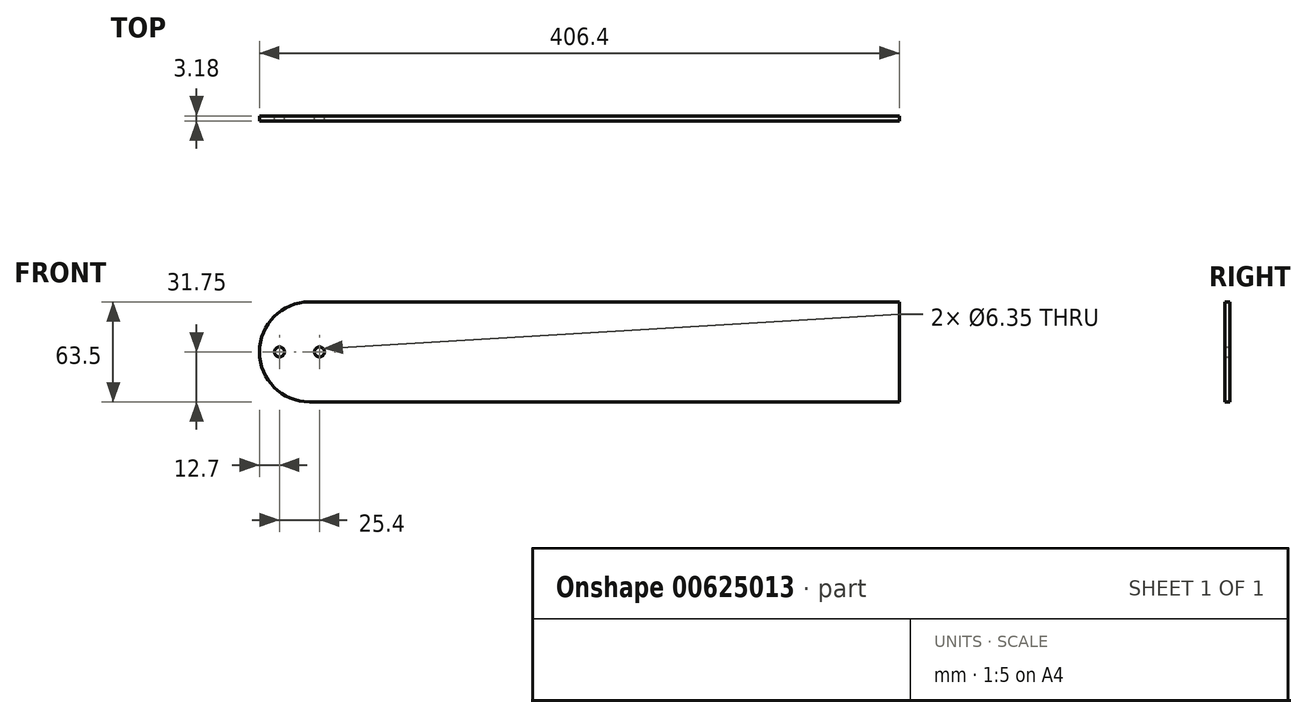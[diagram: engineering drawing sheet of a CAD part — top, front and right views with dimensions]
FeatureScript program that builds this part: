
annotation { "Feature Type Name" : "Feature", "Feature Type Description" : "" }
export const myFeature = defineFeature(function(context is Context, id is Id, definition is map)
    precondition{}
    {
        {
            var Q0;
            Q0=qCreatedBy(makeId("Front.planeOp"),FACE);
            var sketch = newSketch(context, id + "F0", { "sketchPlane" : qUnion([Q0])});
            skLineSegment(sketch, "E0.bottom", {"start": v(31.75, 0) * mm, "end": v(406.4, 0) * mm});
            skLineSegment(sketch, "E0.top", {"start": v(31.75, 63.5) * mm, "end": v(406.4, 63.5) * mm});
            skLineSegment(sketch, "E0.left", {"start": v(0, 31.75) * mm, "end": v(0, 31.75) * mm});
            skLineSegment(sketch, "E0.right", {"start": v(406.4, 0) * mm, "end": v(406.4, 63.5) * mm});
            skLineSegment(sketch, "E1", {"start": v(0, 31.75) * mm, "end": v(38.1, 31.75) * mm});
            skPoint(sketch, "E1.endSnap0", {"position": v(0, 31.75) * mm});
            skCircle(sketch, "E2", {"center": v(38.1, 31.75) * mm, "radius": 3.18 * mm});
            skCircle(sketch, "E3", {"center": v(38.1, 31.75) * mm, "radius": 25.4 * mm});
            skLineSegment(sketch, "E4", {"start": v(12.7, 31.75) * mm, "end": v(38.1, 31.75) * mm});
            skCircle(sketch, "E5", {"center": v(368.3, 31.75) * mm, "radius": 50 * mm});
            skCircle(sketch, "E6", {"center": v(368.3, 81.75) * mm, "radius": 6.35 * mm});
            skCircle(sketch, "E7", {"center": v(368.3, -18.25) * mm, "radius": 6.35 * mm});
            skCircle(sketch, "E8", {"center": v(318.3, 31.75) * mm, "radius": 6.35 * mm});
            skCircle(sketch, "E9", {"center": v(418.3, 31.75) * mm, "radius": 6.35 * mm});
            skPoint(sketch, "E10.visualSharp", {"position": v(0, 63.5) * mm});
            skArc(sketch, "E10.filletArc", {"start": v(31.75, 63.5) * mm, "mid": v(9.3, 54.2) * mm, "end": v(0, 31.75) * mm});
            skPoint(sketch, "E11.visualSharp", {"position": v(0, 0) * mm});
            skArc(sketch, "E11.filletArc", {"start": v(0, 31.75) * mm, "mid": v(9.3, 9.3) * mm, "end": v(31.75, 0) * mm});
            skCircle(sketch, "E12", {"center": v(12.7, 31.75) * mm, "radius": 3.18 * mm});
            skSolve(sketch);
        }
        {
            var Q0;
            {var subQ0=sQuery(id+"F0.wireOp",EDGE,"O3syXbHt-yHTN-aNau-WEg2-3ZSHqx7OYMuC");var subQ3=sQuery(id+"F0.wireOp",EDGE,"E0.top");var subQ4=makeQuery(id+"F0.imprint","INTERSECT",VERTEX,{"disambiguationData":[OD(0.0)],"derivedFrom":[subQ3,subQ0]});Q0=makeQuery(id+"F0.imprint","IMPRINT",FACE,{"disambiguationData":[TD([[makeQuery(id+"F0.imprint","IMPRINT",EDGE,{"disambiguationData":[TD([[subQ4,-1.0]])],"derivedFrom":subQ3}),-1.0]])]});}
            var Q1;
            {var subQ1=sQuery(id+"F0.wireOp",EDGE,"E0.bottom");var subQ5=sQuery(id+"F0.wireOp",EDGE,"O3syXbHt-yHTN-aNau-WEg2-3ZSHqx7OYMuC");var subQ8=makeQuery(id+"F0.imprint","INTERSECT",VERTEX,{"disambiguationData":[OD(0.0)],"derivedFrom":[subQ1,subQ5]});Q1=makeQuery(id+"F0.imprint","IMPRINT",FACE,{"disambiguationData":[TD([[makeQuery(id+"F0.imprint","IMPRINT",EDGE,{"disambiguationData":[TD([[subQ8,-1.0]])],"derivedFrom":subQ1}),1.0]])]});}
            var Q2;
            Q2=makeQuery(id+"F0.imprint","IMPRINT",FACE,{"disambiguationData":[TD([[makeQuery(id+"F0.imprint","IMPRINT",EDGE,{"derivedFrom":sQuery(id+"F0.wireOp",EDGE,"E2")}),-1.0]])]});
            var Q3;
            {var subQ0=sQuery(id+"F0.wireOp",EDGE,"O3syXbHt-yHTN-aNau-WEg2-3ZSHqx7OYMuC");var subQ1=sQuery(id+"F0.wireOp",EDGE,"E0.bottom");var subQ2=makeQuery(id+"F0.imprint","INTERSECT",VERTEX,{"disambiguationData":[OD(1.0)],"derivedFrom":[subQ1,subQ0]});Q3=makeQuery(id+"F0.imprint","IMPRINT",FACE,{"disambiguationData":[TD([[makeQuery(id+"F0.imprint","IMPRINT",EDGE,{"disambiguationData":[TD([[subQ2,1.0]])],"derivedFrom":subQ1}),1.0]])]});}
            var Q4;
            {var subQ0=sQuery(id+"F0.wireOp",EDGE,"O3syXbHt-yHTN-aNau-WEg2-3ZSHqx7OYMuC");var subQ1=sQuery(id+"F0.wireOp",EDGE,"E0.bottom");var subQ2=makeQuery(id+"F0.imprint","INTERSECT",VERTEX,{"disambiguationData":[OD(1.0)],"derivedFrom":[subQ1,subQ0]});Q4=makeQuery(id+"F0.imprint","IMPRINT",FACE,{"disambiguationData":[TD([[makeQuery(id+"F0.imprint","IMPRINT",EDGE,{"disambiguationData":[TD([[subQ2,-1.0]])],"derivedFrom":subQ1}),1.0]])]});}
            var Q5;
            {var subQ5=sQuery(id+"F0.wireOp",EDGE,"E0.right");Q5=makeQuery(id+"F0.imprint","IMPRINT",FACE,{"disambiguationData":[TD([[makeQuery(id+"F0.imprint","IMPRINT",EDGE,{"derivedFrom":subQ5}),1.0]])]});}
            var Q6;
            {var subQ0=sQuery(id+"F0.wireOp",EDGE,"E8");var subQ1=sQuery(id+"F0.wireOp",EDGE,"E5");var subQ2=makeQuery(id+"F0.imprint","INTERSECT",VERTEX,{"disambiguationData":[OD(0.0)],"derivedFrom":[subQ1,subQ0]});Q6=makeQuery(id+"F0.imprint","IMPRINT",FACE,{"disambiguationData":[TD([[makeQuery(id+"F0.imprint","IMPRINT",EDGE,{"disambiguationData":[TD([[subQ2,-1.0]])],"derivedFrom":subQ1}),1.0]])]});}
            var Q7;
            {var subQ0=sQuery(id+"F0.wireOp",EDGE,"E8");var subQ1=sQuery(id+"F0.wireOp",EDGE,"E5");var subQ2=makeQuery(id+"F0.imprint","INTERSECT",VERTEX,{"disambiguationData":[OD(0.0)],"derivedFrom":[subQ1,subQ0]});Q7=makeQuery(id+"F0.imprint","IMPRINT",FACE,{"disambiguationData":[TD([[makeQuery(id+"F0.imprint","IMPRINT",EDGE,{"disambiguationData":[TD([[subQ2,-1.0]])],"derivedFrom":subQ1}),-1.0]])]});}
            var Q8;
            {var subQ11=sQuery(id+"F0.wireOp",EDGE,"E10.filletArc");Q8=makeQuery(id+"F0.imprint","IMPRINT",FACE,{"disambiguationData":[TD([[makeQuery(id+"F0.imprint","IMPRINT",EDGE,{"derivedFrom":subQ11}),1.0]])]});}
            extrude(context, id + "F1", {"entities" : qUnion([Q0, Q1, Q2, Q3, Q4, Q5, Q6, Q7, Q8]), "depth" : 3.17 * mm, "offsetDistance" : 25.4 * mm});
        }
    });
